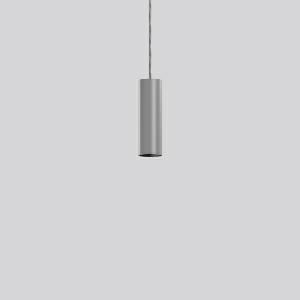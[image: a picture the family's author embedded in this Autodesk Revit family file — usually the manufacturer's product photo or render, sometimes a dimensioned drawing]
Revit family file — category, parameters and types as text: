
# Revit family: deecos_p_micro_911490_004_1_1606
name_source: partatom
category: Lighting Fixtures
units: mm (PartAtom-declared; Revit-internal decimal feet)

## family parameters
Cut with Voids When Loaded = No
Host = Face
Light Source = No
Part Type = Normal
Room Calculation Point = No
Round Connector Dimension = Use Diameter
Shared = No

## types (1)
- DEECOS P micro (1 x LED Modul 930, 1250 lm, 3000)
    Apparent Load = 16 VA
    CIE Flux Codes = 92 99 100 100 100
    Color Rendering = 90
    Color Temperature = 3000
    Default Elevation = 1800 mm
    Description = Series: DEECOS P micro
Cylindrical pendant luminaire. Housing: die-cast aluminium, powder-coated. Canopy made of powder-coated sheet steel with magnetic attachment. Optical assembly with lens made of plastic (polycarbonate) for the best homogeneous light distribution - can be changed without tools. Black plastic ring and recessed LED to prevent glare from the side. Best colour rendering index Ra>90. Transparent suspension cable 3 m, can be shortened. High quality converter without flickering and stroboscopic effect. 
Colour: silver
Diameter: 60 mm
Height: 190 mm
Suspension length: 3000 mm
Lamp: LED
Socket: without socket
Colour temperature: 3000K
Colour rendering index (CRI): 92
System power: 16 W
Rated luminous flux: 1250 lm
Luminous efficiency: 78 lm/W
Control gear: Regulated power supply
Protection class: I
Type of protection: IP 20
    Height = 190 mm  [stored 0.62336 ft]
    Lamp = 1 x LED Modul 930
    Lamp Light Flux = 1250 lm
    Lamp count = 1
    Length = 60 mm  [stored 0.19685 ft]
    Lifetime = 50000 h
    Luminous efficacy = 78 lm/W
    Manufacturer = RZB
    ModVariant = No
    Model = 911490.004.1
    Mounting Place = Ceiling
    Mounting Type = Pendant
    Number of Poles = 1
    OnlyDefault = Yes
    Power Factor = 1
    Product Name = DEECOS P micro
    Product group = Pendant luminaires
    ProductGroupID = 902
    Protection Class = Protection class I
    Protection Degree = Degree of protection
    RLX_Detail_Level = 1
    RLX_Emergency_Light_Flux = 0 lm
    RLX_Emergency_Type = 0
    RLX_Emergency_Type_DB = No
    RlxData = <blob elided: 31045 chars, md5=2aadd412>
    Socket = socket
    Standby Power = 0 W
    System Light Flux = 1250 lm
    System Power = 16 W
    Type Comments = Product without accessories
    Type Image = 911489.004.jpg
    URL = http://relux.com
    VarID = ---
    Voltage = 0 V
    Weight = 0.00 kg
    Width = 0 mm  [stored 0 ft]

note: [stored X ft] marks values corroborated as IEEE doubles in the binary element streams (Revit-internal decimal feet)

## geometry (parser evidence)
native form markers: Blend x4, Sweep x10
no freeform markers — native parametric forms only
